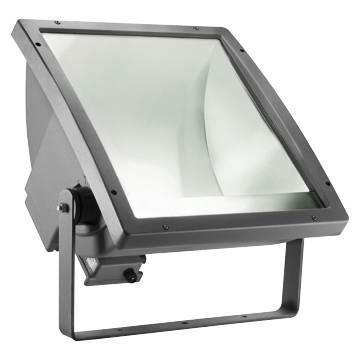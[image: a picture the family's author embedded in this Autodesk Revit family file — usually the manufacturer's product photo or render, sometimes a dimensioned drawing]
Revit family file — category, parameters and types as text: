
# Revit family: Lighting-Floodlights-GEWISS-STADIUM-OPTIC-ASYMMETRICAL
name_source: partatom
category: Apparecchi per illuminazione
units: mm (PartAtom-declared; Revit-internal decimal feet)

## family parameters
Condiviso = No
Host = Superficie
Numero OmniClass = 23.80.70.00
Punto di calcolo locali = Sì
Quota connettore circolare = Usa diametro
Sorgente d'illuminazione = No
Taglio con vuoti quando caricato = No
Tipo di parte = Normale
Titolo OmniClass = Lighting

## types (2) — shared parameters
Application = External
Carico apparente = 1000 VA
Catalogue = LIGHTING
Catalogue Range = STADIUM
Colour = Graphite grey
Commenti sul wattaggio = 1000W
Electrocod = 2433
H_Centro rotazione = 296 mm  [stored 0.971129 ft]
IDF = ce56a893-a50b-4a91-8a9e-10dcb1aad73c
IDT = e7e0fa0a-f0d4-43c6-8d95-65bc926b836b
IP degree = IP66
Immagine tipo = GW84667.jpg
Insulation class = I
L_interna staffa = 612 mm  [stored 2.00787 ft]
Lamp = MN
Lamp holder = X528/CABLE
Lampada = MN
Lateral surface exposed to the wind = 0,141M2
Light pollution = 0 cd/Klm
Lunghezza proiettore = 604 mm  [stored 1.98163 ft]
Material = Aluminium
Maximum surface exposed to the wind = 0,392M2
Minimum distance from the illuminated object = 3M
Numero di poli = 2
Optic = Asymmetrical - ULOR: 0%
Produttore = GEWISS S.p.A.
Prospetto di default = 1219 mm
SEO = Floodlight
Shock resistance = IK09
Technical sheet = https://www.gewiss.com
URL = https://www.gewiss.com
Version file RFA = 20.11
Voltaggio = 230 V

## per-type parameters (varying)
| type | Descrizione | EAN code | Lamp current | Lamp current: | Lamp power | Modello | Weight (kg) | Weight (kg): |
| GW84668 - STADIUM ASY. 2000W MN X528/CABLE | STADIUM ASY. 2000W MN X528/CABLE | 8011564252325 | 10,3A | 10,3A | 2000W | GW84668 | 23,5 | 23,5 |
| GW84667 - STADIUM ASY. 1000W MN X528/CABLE | STADIUM ASY. 1000W MN X528/CABLE | 8011564252318 | 9,5A | 9,5A | 1000W | GW84667 | 24,1 | 24,1 |

note: [stored X ft] marks values corroborated as IEEE doubles in the binary element streams (Revit-internal decimal feet)

## geometry (parser evidence)
native form markers: Blend x393
no freeform markers — native parametric forms only
